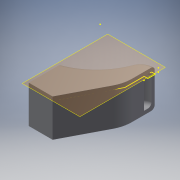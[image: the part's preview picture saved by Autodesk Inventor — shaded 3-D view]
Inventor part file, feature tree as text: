
AUTODESK INVENTOR PART (.ipt)
format: ipt  version: 2016 (Build 200138000, 138)  size: 250,368 bytes
history: native  units: mm
features: sketch x7, fillet x5, reference x5, extrude x4, plane x1, chamfer x1, shell x1, move_body x1, projected_geometry x1
ambient origin geometry x8: Origin, YZ Plane, XZ Plane, XY Plane, X Axis, Y Axis, Z Axis, Center Point
bodies: Solid1 (feature_tree)
feature tree (26):
  plane  "Work Plane1"
  extrude  "Extrusion1"  Depth=25.0mm TaperAngle=45.0deg
  chamfer  "Chamfer1"  Distance=2.0mm
  sketch  "Sketch2"  dims[d5=2.0mm]
  shell  "Shell1"  Thickness=3.0mm
  extrude  "Extrusion2"  Depth=2.0mm
  sketch  "Sketch4"  dims[d10=5.5mm d11=2.0mm d12=17.25mm d13=4.0mm d14=16.0mm d15=0.0mm d16=2.0mm d17=0.0mm]
  sketch  "Sketch5"  dims[d18=-2.0mm d19=0.0mm d20=0.0mm]
  fillet  "Fillet1"  Radius=17.25mm
  fillet  "Fillet2"  Radius=4.0mm
  fillet  "Fillet3"  Radius=16.0mm
  fillet  "Fillet4"  Radius=2.0mm
  fillet  "Fillet5"  [1 undecoded]
  extrude  "Extrusion3"  [1 undecoded]
  extrude  "Extrusion4"  [1 undecoded]
  move_body  "Move Body1"
  sketch  "Sketch1"  dims[d0=20.0mm d1=0.0mm d2=25.0mm d3=13.0mm d4=45.0deg]
  sketch  "Sketch3"  dims[d6=8.0mm d7=2.0mm d8=0.0mm d9=3.0mm]
  reference  "Reference1"
  projected_geometry  "Projected Loop1"
  sketch  "Sketch6"
  reference  "Reference2"
  reference  "Reference3"
  reference  "Reference4"
  reference  "Reference5"
  sketch  "Sketch7"
note: 3 required parameter values undecoded (feature->parameter linkage not recoverable at this tier; creation-order binding heuristic only, values carry confidence <= 0.55)
